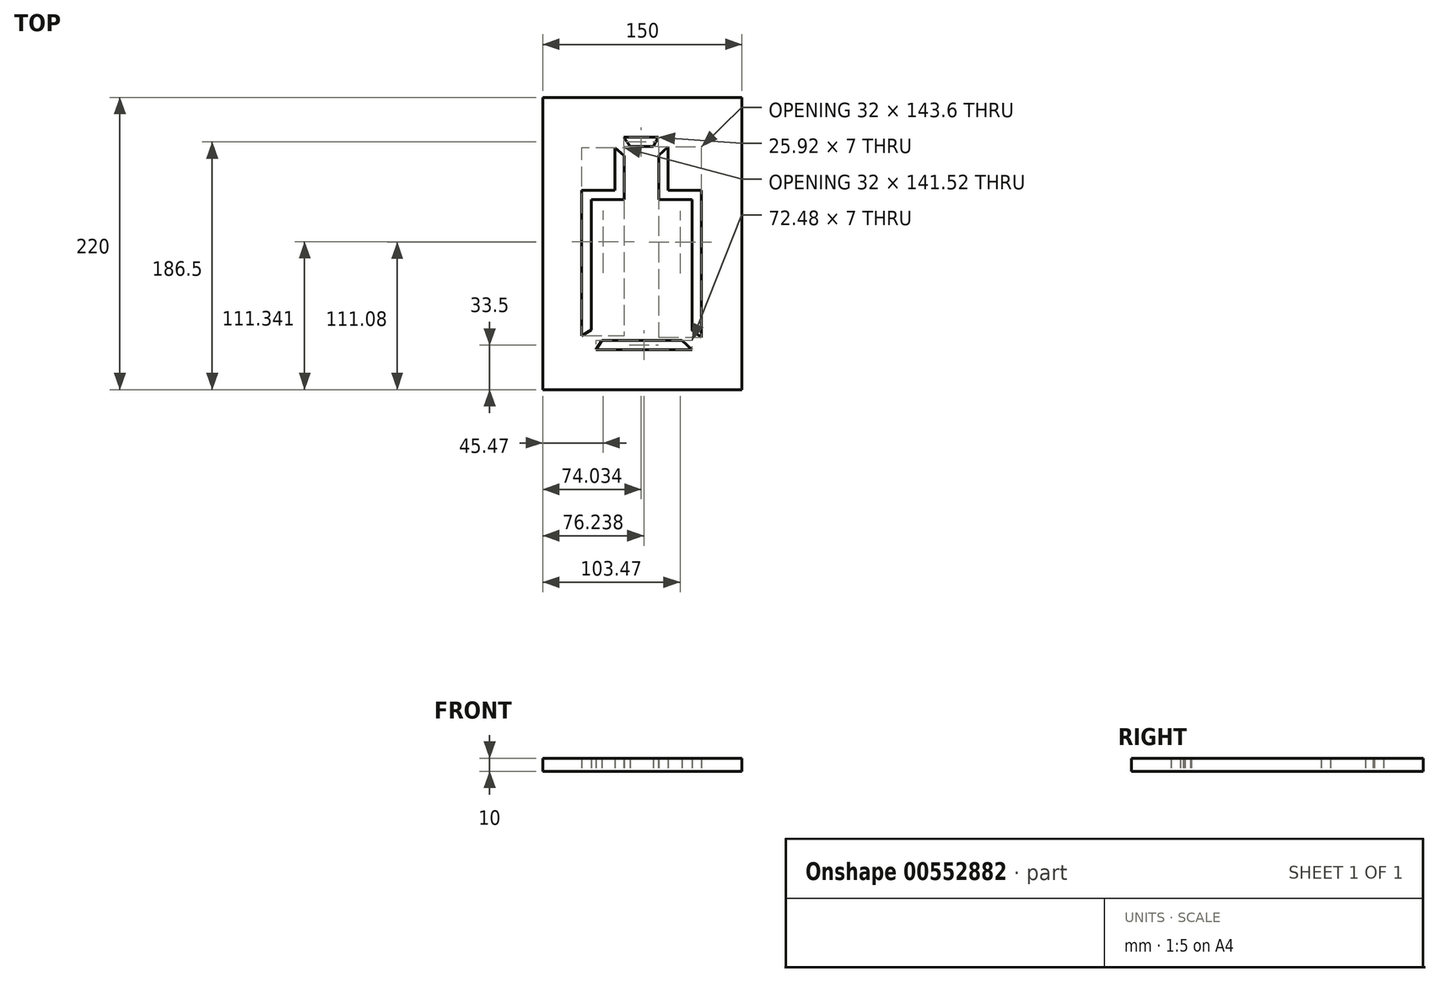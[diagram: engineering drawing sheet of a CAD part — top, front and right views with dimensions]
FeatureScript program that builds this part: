
annotation { "Feature Type Name" : "Feature", "Feature Type Description" : "" }
export const myFeature = defineFeature(function(context is Context, id is Id, definition is map)
    precondition{}
    {
        {
            var Q0;
            Q0=qCreatedBy(makeId("Top.planeOp"),FACE);
            var sketch = newSketch(context, id + "F0", { "sketchPlane" : qUnion([Q0])});
            skLineSegment(sketch, "E0.bottom", {"start": v(10.53, 0) * mm, "end": v(83.01, 0) * mm});
            skLineSegment(sketch, "E0.top", {"start": v(0, 120) * mm, "end": v(25, 120) * mm});
            skLineSegment(sketch, "E0.left", {"start": v(0, 10.58) * mm, "end": v(0, 120) * mm});
            skLineSegment(sketch, "E0.right", {"start": v(90, 9.28) * mm, "end": v(90, 120) * mm});
            skLineSegment(sketch, "E1", {"start": v(25, 120) * mm, "end": v(25, 152.1) * mm});
            skLineSegment(sketch, "E2", {"start": v(31.6, 160) * mm, "end": v(57.52, 160) * mm});
            skLineSegment(sketch, "E3", {"start": v(65, 152.88) * mm, "end": v(65, 120) * mm});
            skLineSegment(sketch, "E4.trimOffspring", {"start": v(65, 120) * mm, "end": v(90, 120) * mm});
            skLineSegment(sketch, "E5.0", {"start": v(7, 15.1) * mm, "end": v(7, 113) * mm});
            skLineSegment(sketch, "E5.1", {"start": v(15, 7) * mm, "end": v(75.5, 7) * mm});
            skLineSegment(sketch, "E5.2", {"start": v(7, 113) * mm, "end": v(32, 113) * mm});
            skLineSegment(sketch, "E5.3", {"start": v(83, 14.64) * mm, "end": v(83, 113) * mm});
            skLineSegment(sketch, "E5.4", {"start": v(32, 113) * mm, "end": v(32, 146.24) * mm});
            skLineSegment(sketch, "E5.6", {"start": v(58, 146.4) * mm, "end": v(58, 113) * mm});
            skLineSegment(sketch, "E5.7", {"start": v(58, 113) * mm, "end": v(83, 113) * mm});
            skLineSegment(sketch, "E6", {"start": v(32, 146.24) * mm, "end": v(25, 152.1) * mm});
            skLineSegment(sketch, "E7", {"start": v(36.33, 153) * mm, "end": v(31.6, 160) * mm});
            skLineSegment(sketch, "E8", {"start": v(53.75, 153) * mm, "end": v(57.52, 160) * mm});
            skLineSegment(sketch, "E9", {"start": v(58, 146.4) * mm, "end": v(65, 152.88) * mm});
            skLineSegment(sketch, "E10", {"start": v(83.01, 0) * mm, "end": v(75.5, 7) * mm});
            skLineSegment(sketch, "E11", {"start": v(83, 14.64) * mm, "end": v(90, 9.28) * mm});
            skLineSegment(sketch, "E12", {"start": v(10.53, 0) * mm, "end": v(15, 7) * mm});
            skLineSegment(sketch, "E13", {"start": v(7, 15.1) * mm, "end": v(0, 10.58) * mm});
            skLineSegment(sketch, "E14", {"start": v(36.33, 153) * mm, "end": v(53.75, 153) * mm});
            skSolve(sketch);
        }
        {
            var Q0;
            Q0=qCreatedBy(makeId("Top.planeOp"),FACE);
            var sketch = newSketch(context, id + "F1", { "sketchPlane" : qUnion([Q0])});
            skLineSegment(sketch, "E15.bottom", {"start": v(-29.47, -30) * mm, "end": v(120.53, -30) * mm});
            skLineSegment(sketch, "E15.top", {"start": v(-29.47, 190) * mm, "end": v(120.53, 190) * mm});
            skLineSegment(sketch, "E15.left", {"start": v(-29.47, -30) * mm, "end": v(-29.47, 190) * mm});
            skLineSegment(sketch, "E15.right", {"start": v(120.53, -30) * mm, "end": v(120.53, 190) * mm});
            skSolve(sketch);
        }
        {
            var Q0;
            Q0 = qSketchRegion(id + "F1", true);
            extrude(context, id + "F2", {"entities" : qUnion([Q0]), "depth" : 10 * mm, "offsetDistance" : 25 * mm});
        }
        {
            var Q0;
            Q0 = qSketchRegion(id + "F0", true);
            extrude(context, id + "F3", {"entities" : qUnion([Q0]), "operationType" : NewBodyOperationType.REMOVE, "depth" : 25 * mm, "offsetDistance" : 25 * mm});
        }
    });
